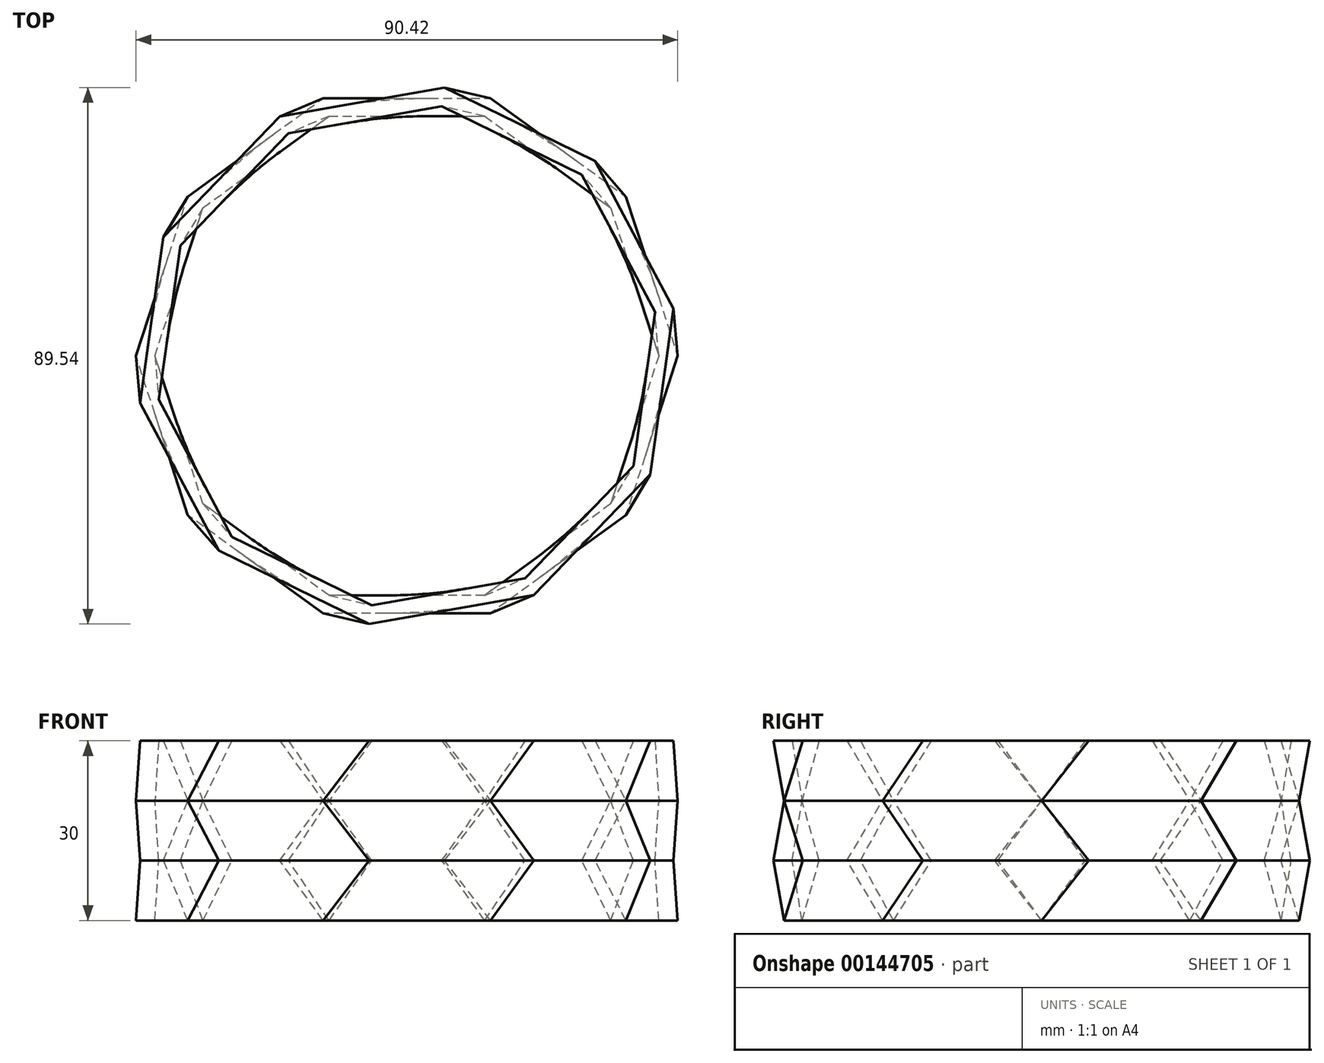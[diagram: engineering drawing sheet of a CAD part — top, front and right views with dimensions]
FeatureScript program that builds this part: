
annotation { "Feature Type Name" : "Feature", "Feature Type Description" : "" }
export const myFeature = defineFeature(function(context is Context, id is Id, definition is map)
    precondition{}
    {
        {
            var Q0;
            Q0=qCreatedBy(makeId("Top.planeOp"),FACE);
            var sketch = newSketch(context, id + "F0", { "sketchPlane" : qUnion([Q0])});
            skCircle(sketch, "E0.cCircle", {"center": v(0, 0) * mm, "radius": 40 * mm, "construction": true});
            skLineSegment(sketch, "E0.0", {"start": v(-13, 40) * mm, "end": v(13, 40) * mm});
            skLineSegment(sketch, "E0.1", {"start": v(13, 40) * mm, "end": v(34.03, 24.72) * mm});
            skLineSegment(sketch, "E0.2", {"start": v(34.03, 24.72) * mm, "end": v(42.06, 0) * mm});
            skLineSegment(sketch, "E0.3", {"start": v(42.06, 0) * mm, "end": v(34.03, -24.72) * mm});
            skLineSegment(sketch, "E0.4", {"start": v(34.03, -24.72) * mm, "end": v(13, -40) * mm});
            skLineSegment(sketch, "E0.5", {"start": v(13, -40) * mm, "end": v(-13, -40) * mm});
            skLineSegment(sketch, "E0.6", {"start": v(-13, -40) * mm, "end": v(-34.03, -24.72) * mm});
            skLineSegment(sketch, "E0.7", {"start": v(-34.03, -24.72) * mm, "end": v(-42.06, 0) * mm});
            skLineSegment(sketch, "E0.8", {"start": v(-42.06, 0) * mm, "end": v(-34.03, 24.72) * mm});
            skLineSegment(sketch, "E0.9", {"start": v(-34.03, 24.72) * mm, "end": v(-13, 40) * mm});
            skPoint(sketch, "E0.0.midPoint", {"position": v(0, 40) * mm});
            skSolve(sketch);
        }
        {
            var Q0;
            Q0=qCreatedBy(makeId("Top.planeOp"),FACE);
            var sketch = newSketch(context, id + "F1", { "sketchPlane" : qUnion([Q0])});
            skLineSegment(sketch, "E1.0", {"start": v(-36.58, 26.58) * mm, "end": v(-13.97, 43) * mm});
            skLineSegment(sketch, "E1.1", {"start": v(-45.21, 0) * mm, "end": v(-36.58, 26.58) * mm});
            skLineSegment(sketch, "E1.2", {"start": v(-13.97, 43) * mm, "end": v(13.97, 43) * mm});
            skLineSegment(sketch, "E1.3", {"start": v(-36.58, -26.58) * mm, "end": v(-45.21, 0) * mm});
            skLineSegment(sketch, "E1.4", {"start": v(-13.97, -43) * mm, "end": v(-36.58, -26.58) * mm});
            skLineSegment(sketch, "E1.5", {"start": v(13.97, -43) * mm, "end": v(-13.97, -43) * mm});
            skLineSegment(sketch, "E1.6", {"start": v(13.97, 43) * mm, "end": v(36.58, 26.58) * mm});
            skLineSegment(sketch, "E1.7", {"start": v(36.58, 26.58) * mm, "end": v(45.21, 0) * mm});
            skLineSegment(sketch, "E1.8", {"start": v(45.21, 0) * mm, "end": v(36.58, -26.58) * mm});
            skLineSegment(sketch, "E1.9", {"start": v(36.58, -26.58) * mm, "end": v(13.97, -43) * mm});
            skSolve(sketch);
        }
        {
            var Q0;
            Q0=makeQuery(id+"F1.imprint","IMPRINT",FACE,{"disambiguationData":[TD([[makeQuery(id+"F1.imprint","IMPRINT",EDGE,{"derivedFrom":sQuery(id+"F1.wireOp",EDGE,"E1.0")}),-1.0]])]});
            cPlane(context, id + "F2", {"entities" : qUnion([Q0]), "cplaneType" : CPlaneType.OFFSET, "offset" : 10 * mm, "width" : 150 * mm, "height" : 150 * mm});
        }
        {
            var Q0;
            Q0=qCreatedBy(id+"F2.planeOp",FACE);
            var sketch = newSketch(context, id + "F3", { "sketchPlane" : qUnion([Q0])});
            skCircle(sketch, "E2.cCircle", {"center": v(0, 0) * mm, "radius": 40 * mm, "construction": true});
            skLineSegment(sketch, "E2.0", {"start": v(-5.85, -41.65) * mm, "end": v(-29.22, -30.25) * mm});
            skLineSegment(sketch, "E2.1", {"start": v(-29.22, -30.25) * mm, "end": v(-41.42, -7.3) * mm});
            skLineSegment(sketch, "E2.2", {"start": v(-41.42, -7.3) * mm, "end": v(-37.8, 18.44) * mm});
            skLineSegment(sketch, "E2.3", {"start": v(-37.8, 18.44) * mm, "end": v(-19.75, 37.14) * mm});
            skLineSegment(sketch, "E2.4", {"start": v(-19.75, 37.14) * mm, "end": v(5.85, 41.65) * mm});
            skLineSegment(sketch, "E2.5", {"start": v(5.85, 41.65) * mm, "end": v(29.22, 30.25) * mm});
            skLineSegment(sketch, "E2.6", {"start": v(29.22, 30.25) * mm, "end": v(41.42, 7.3) * mm});
            skLineSegment(sketch, "E2.7", {"start": v(41.42, 7.3) * mm, "end": v(37.8, -18.44) * mm});
            skLineSegment(sketch, "E2.8", {"start": v(37.8, -18.44) * mm, "end": v(19.75, -37.14) * mm});
            skLineSegment(sketch, "E2.9", {"start": v(19.75, -37.14) * mm, "end": v(-5.85, -41.65) * mm});
            skPoint(sketch, "E2.0.midPoint", {"position": v(-17.53, -35.95) * mm});
            skSolve(sketch);
        }
        {
            var Q0;
            Q0=qCreatedBy(id+"F2.planeOp",FACE);
            var sketch = newSketch(context, id + "F4", { "sketchPlane" : qUnion([Q0])});
            skLineSegment(sketch, "E3.0", {"start": v(-40.64, 19.82) * mm, "end": v(-21.23, 39.92) * mm});
            skLineSegment(sketch, "E3.1", {"start": v(-44.53, -7.85) * mm, "end": v(-40.64, 19.82) * mm});
            skLineSegment(sketch, "E3.2", {"start": v(-21.23, 39.92) * mm, "end": v(6.3, 44.77) * mm});
            skLineSegment(sketch, "E3.3", {"start": v(-31.4, -32.52) * mm, "end": v(-44.53, -7.85) * mm});
            skLineSegment(sketch, "E3.4", {"start": v(-6.3, -44.77) * mm, "end": v(-31.4, -32.52) * mm});
            skLineSegment(sketch, "E3.5", {"start": v(21.23, -39.92) * mm, "end": v(-6.3, -44.77) * mm});
            skLineSegment(sketch, "E3.6", {"start": v(6.3, 44.77) * mm, "end": v(31.4, 32.52) * mm});
            skLineSegment(sketch, "E3.7", {"start": v(31.4, 32.52) * mm, "end": v(44.53, 7.85) * mm});
            skLineSegment(sketch, "E3.8", {"start": v(44.53, 7.85) * mm, "end": v(40.64, -19.82) * mm});
            skLineSegment(sketch, "E3.9", {"start": v(40.64, -19.82) * mm, "end": v(21.23, -39.92) * mm});
            skSolve(sketch);
        }
        {
            var Q0;
            Q0=makeQuery(id+"F0.imprint","IMPRINT",FACE,{"disambiguationData":[TD([[makeQuery(id+"F0.imprint","IMPRINT",EDGE,{"derivedFrom":sQuery(id+"F0.wireOp",EDGE,"E0.0")}),-1.0]])]});
            var Q1;
            Q1=makeQuery(id+"F3.imprint","IMPRINT",FACE,{"disambiguationData":[TD([[makeQuery(id+"F3.imprint","IMPRINT",EDGE,{"derivedFrom":sQuery(id+"F3.wireOp",EDGE,"E2.0")}),-1.0]])]});
            loft(context, id + "F5", {"sheetProfilesArray" : [{ "sheetProfileEntities" : qUnion([Q0]) }, { "sheetProfileEntities" : qUnion([Q1]) }]});
        }
        {
            var Q1;
            Q1=makeQuery(id+"F1.imprint","IMPRINT",FACE,{"disambiguationData":[TD([[makeQuery(id+"F1.imprint","IMPRINT",EDGE,{"derivedFrom":sQuery(id+"F1.wireOp",EDGE,"E1.0")}),-1.0]])]});
            var Q2;
            Q2=makeQuery(id+"F4.imprint","IMPRINT",FACE,{"disambiguationData":[TD([[makeQuery(id+"F4.imprint","IMPRINT",EDGE,{"derivedFrom":sQuery(id+"F4.wireOp",EDGE,"E3.0")}),-1.0]])]});
            loft(context, id + "F6", {"sheetProfilesArray" : [{ "sheetProfileEntities" : qUnion([Q1]) }, { "sheetProfileEntities" : qUnion([Q2]) }]});
        }
        {
            var Q0;
            Q0=makeQuery(id+"F5.opLoft","SWEPT_BODY",BODY,{"disambiguationData":[OSD([makeQuery(id+"F0.imprint","IMPRINT",FACE,{"disambiguationData":[TD([[makeQuery(id+"F0.imprint","IMPRINT",EDGE,{"derivedFrom":sQuery(id+"F0.wireOp",EDGE,"E0.0")}),-1.0]])]}),makeQuery(id+"F3.imprint","IMPRINT",FACE,{"disambiguationData":[TD([[makeQuery(id+"F3.imprint","IMPRINT",EDGE,{"derivedFrom":sQuery(id+"F3.wireOp",EDGE,"E2.0")}),-1.0]])]})])]});
            var Q1;
            Q1=makeQuery(id+"F6.opLoft","SWEPT_BODY",BODY,{"disambiguationData":[OSD([makeQuery(id+"F1.imprint","IMPRINT",FACE,{"disambiguationData":[TD([[makeQuery(id+"F1.imprint","IMPRINT",EDGE,{"derivedFrom":sQuery(id+"F1.wireOp",EDGE,"E1.0")}),-1.0]])]}),makeQuery(id+"F4.imprint","IMPRINT",FACE,{"disambiguationData":[TD([[makeQuery(id+"F4.imprint","IMPRINT",EDGE,{"derivedFrom":sQuery(id+"F4.wireOp",EDGE,"E3.0")}),-1.0]])]})])]});
            booleanBodies(context, id + "F7", {"operationType" : BooleanOperationType.SUBTRACTION, "tools" : qUnion([Q0]), "targets" : qUnion([Q1])});
        }
        {
            var Q0;
            Q0=makeQuery(id+"F6.opLoft","CAP_FACE",FACE,{"disambiguationData":[OSD([makeQuery(id+"F4.imprint","IMPRINT",FACE,{"disambiguationData":[TD([[makeQuery(id+"F4.imprint","IMPRINT",EDGE,{"derivedFrom":sQuery(id+"F4.wireOp",EDGE,"E3.0")}),-1.0]])]})])],"isStart":true});
            cPlane(context, id + "F8", {"entities" : qUnion([Q0]), "cplaneType" : CPlaneType.OFFSET, "offset" : 10 * mm, "width" : 150 * mm, "height" : 150 * mm});
        }
        {
            var Q0;
            Q0=qCreatedBy(id+"F8.planeOp",FACE);
            var sketch = newSketch(context, id + "F9", { "sketchPlane" : qUnion([Q0])});
            skCircle(sketch, "E4.cCircle", {"center": v(0, 0) * mm, "radius": 40 * mm, "construction": true});
            skLineSegment(sketch, "E4.0", {"start": v(-13, 40) * mm, "end": v(13, 40) * mm});
            skLineSegment(sketch, "E4.1", {"start": v(13, 40) * mm, "end": v(34.03, 24.72) * mm});
            skLineSegment(sketch, "E4.2", {"start": v(34.03, 24.72) * mm, "end": v(42.06, 0) * mm});
            skLineSegment(sketch, "E4.3", {"start": v(42.06, 0) * mm, "end": v(34.03, -24.72) * mm});
            skLineSegment(sketch, "E4.4", {"start": v(34.03, -24.72) * mm, "end": v(13, -40) * mm});
            skLineSegment(sketch, "E4.5", {"start": v(13, -40) * mm, "end": v(-13, -40) * mm});
            skLineSegment(sketch, "E4.6", {"start": v(-13, -40) * mm, "end": v(-34.03, -24.72) * mm});
            skLineSegment(sketch, "E4.7", {"start": v(-34.03, -24.72) * mm, "end": v(-42.06, 0) * mm});
            skLineSegment(sketch, "E4.8", {"start": v(-42.06, 0) * mm, "end": v(-34.03, 24.72) * mm});
            skLineSegment(sketch, "E4.9", {"start": v(-34.03, 24.72) * mm, "end": v(-13, 40) * mm});
            skPoint(sketch, "E4.0.midPoint", {"position": v(0, 40) * mm});
            skSolve(sketch);
        }
        {
            var Q0;
            Q0=qCreatedBy(id+"F8.planeOp",FACE);
            var sketch = newSketch(context, id + "F10", { "sketchPlane" : qUnion([Q0])});
            skLineSegment(sketch, "E5.0", {"start": v(-36.58, 26.58) * mm, "end": v(-13.97, 43) * mm});
            skLineSegment(sketch, "E5.1", {"start": v(-45.21, 0) * mm, "end": v(-36.58, 26.58) * mm});
            skLineSegment(sketch, "E5.2", {"start": v(-13.97, 43) * mm, "end": v(13.97, 43) * mm});
            skLineSegment(sketch, "E5.3", {"start": v(-36.58, -26.58) * mm, "end": v(-45.21, 0) * mm});
            skLineSegment(sketch, "E5.4", {"start": v(-13.97, -43) * mm, "end": v(-36.58, -26.58) * mm});
            skLineSegment(sketch, "E5.5", {"start": v(13.97, -43) * mm, "end": v(-13.97, -43) * mm});
            skLineSegment(sketch, "E5.6", {"start": v(13.97, 43) * mm, "end": v(36.58, 26.58) * mm});
            skLineSegment(sketch, "E5.7", {"start": v(36.58, 26.58) * mm, "end": v(45.21, 0) * mm});
            skLineSegment(sketch, "E5.8", {"start": v(45.21, 0) * mm, "end": v(36.58, -26.58) * mm});
            skLineSegment(sketch, "E5.9", {"start": v(36.58, -26.58) * mm, "end": v(13.97, -43) * mm});
            skSolve(sketch);
        }
        {
            var Q0;
            Q0=makeQuery(id+"F4.imprint","IMPRINT",FACE,{"disambiguationData":[TD([[makeQuery(id+"F4.imprint","IMPRINT",EDGE,{"derivedFrom":sQuery(id+"F4.wireOp",EDGE,"E3.0")}),-1.0]])]});
            var sketch = newSketch(context, id + "F11", { "sketchPlane" : qUnion([Q0])});
            skLineSegment(sketch, "E6.0", {"start": v(-31.4, -32.52) * mm, "end": v(-44.53, -7.85) * mm});
            skLineSegment(sketch, "E7.0", {"start": v(-6.3, -44.77) * mm, "end": v(-31.4, -32.52) * mm});
            skLineSegment(sketch, "E8.0", {"start": v(21.23, -39.92) * mm, "end": v(-6.3, -44.77) * mm});
            skLineSegment(sketch, "E9.0", {"start": v(40.64, -19.82) * mm, "end": v(21.23, -39.92) * mm});
            skLineSegment(sketch, "E10.0", {"start": v(44.53, 7.85) * mm, "end": v(40.64, -19.82) * mm});
            skLineSegment(sketch, "E11.0", {"start": v(31.4, 32.52) * mm, "end": v(44.53, 7.85) * mm});
            skLineSegment(sketch, "E12.0", {"start": v(6.3, 44.77) * mm, "end": v(31.4, 32.52) * mm});
            skLineSegment(sketch, "E13.0", {"start": v(-21.23, 39.92) * mm, "end": v(6.3, 44.77) * mm});
            skLineSegment(sketch, "E14.0", {"start": v(-40.64, 19.82) * mm, "end": v(-21.23, 39.92) * mm});
            skLineSegment(sketch, "E15.0", {"start": v(-44.53, -7.85) * mm, "end": v(-40.64, 19.82) * mm});
            skSolve(sketch);
        }
        {
            var Q0;
            Q0=qCreatedBy(id+"F2.planeOp",FACE);
            var sketch = newSketch(context, id + "F12", { "sketchPlane" : qUnion([Q0])});
            skLineSegment(sketch, "E16.0", {"start": v(-37.8, 18.44) * mm, "end": v(-41.42, -7.3) * mm});
            skLineSegment(sketch, "E17.0", {"start": v(-19.75, 37.14) * mm, "end": v(-37.8, 18.44) * mm});
            skLineSegment(sketch, "E18.0", {"start": v(29.22, 30.25) * mm, "end": v(5.85, 41.65) * mm});
            skLineSegment(sketch, "E19.0", {"start": v(5.85, 41.65) * mm, "end": v(-19.75, 37.14) * mm});
            skLineSegment(sketch, "E20.0", {"start": v(41.42, 7.3) * mm, "end": v(29.22, 30.25) * mm});
            skLineSegment(sketch, "E21.0", {"start": v(37.8, -18.44) * mm, "end": v(41.42, 7.3) * mm});
            skLineSegment(sketch, "E22.0", {"start": v(19.75, -37.14) * mm, "end": v(37.8, -18.44) * mm});
            skLineSegment(sketch, "E23.0", {"start": v(-5.85, -41.65) * mm, "end": v(19.75, -37.14) * mm});
            skLineSegment(sketch, "E24.0", {"start": v(-29.22, -30.25) * mm, "end": v(-5.85, -41.65) * mm});
            skLineSegment(sketch, "E25.0", {"start": v(-41.42, -7.3) * mm, "end": v(-29.22, -30.25) * mm});
            skSolve(sketch);
        }
        {
            var Q0;
            Q0=makeQuery(id+"F12.imprint","IMPRINT",FACE,{"disambiguationData":[TD([[makeQuery(id+"F12.imprint","IMPRINT",EDGE,{"derivedFrom":sQuery(id+"F12.wireOp",EDGE,"E16.0")}),1.0]])]});
            var Q1;
            Q1=makeQuery(id+"F9.imprint","IMPRINT",FACE,{"disambiguationData":[TD([[makeQuery(id+"F9.imprint","IMPRINT",EDGE,{"derivedFrom":sQuery(id+"F9.wireOp",EDGE,"E4.0")}),-1.0]])]});
            loft(context, id + "F13", {"sheetProfilesArray" : [{ "sheetProfileEntities" : qUnion([Q0]) }, { "sheetProfileEntities" : qUnion([Q1]) }]});
        }
        {
            var Q0;
            Q0=makeQuery(id+"F11.imprint","IMPRINT",FACE,{"disambiguationData":[TD([[makeQuery(id+"F11.imprint","IMPRINT",EDGE,{"derivedFrom":sQuery(id+"F11.wireOp",EDGE,"E7.0")}),-1.0]])]});
            var Q1;
            Q1=makeQuery(id+"F10.imprint","IMPRINT",FACE,{"disambiguationData":[TD([[makeQuery(id+"F10.imprint","IMPRINT",EDGE,{"derivedFrom":sQuery(id+"F10.wireOp",EDGE,"E5.0")}),-1.0]])]});
            loft(context, id + "F14", {"sheetProfilesArray" : [{ "sheetProfileEntities" : qUnion([Q0]) }, { "sheetProfileEntities" : qUnion([Q1]) }]});
        }
        {
            var Q0;
            Q0=makeQuery(id+"F13.opLoft","SWEPT_BODY",BODY,{"disambiguationData":[OSD([makeQuery(id+"F9.imprint","IMPRINT",FACE,{"disambiguationData":[TD([[makeQuery(id+"F9.imprint","IMPRINT",EDGE,{"derivedFrom":sQuery(id+"F9.wireOp",EDGE,"E4.0")}),-1.0]])]}),makeQuery(id+"F12.imprint","IMPRINT",FACE,{"disambiguationData":[TD([[makeQuery(id+"F12.imprint","IMPRINT",EDGE,{"derivedFrom":sQuery(id+"F12.wireOp",EDGE,"E16.0")}),1.0]])]})])]});
            var Q1;
            Q1=makeQuery(id+"F14.opLoft","SWEPT_BODY",BODY,{"disambiguationData":[OSD([makeQuery(id+"F10.imprint","IMPRINT",FACE,{"disambiguationData":[TD([[makeQuery(id+"F10.imprint","IMPRINT",EDGE,{"derivedFrom":sQuery(id+"F10.wireOp",EDGE,"E5.0")}),-1.0]])]}),makeQuery(id+"F11.imprint","IMPRINT",FACE,{"disambiguationData":[TD([[makeQuery(id+"F11.imprint","IMPRINT",EDGE,{"derivedFrom":sQuery(id+"F11.wireOp",EDGE,"E7.0")}),-1.0]])]})])]});
            booleanBodies(context, id + "F15", {"operationType" : BooleanOperationType.SUBTRACTION, "tools" : qUnion([Q0]), "targets" : qUnion([Q1])});
        }
        {
            var Q0;
            Q0=makeQuery(id+"F14.opLoft","SWEPT_BODY",BODY,{"disambiguationData":[OSD([makeQuery(id+"F10.imprint","IMPRINT",FACE,{"disambiguationData":[TD([[makeQuery(id+"F10.imprint","IMPRINT",EDGE,{"derivedFrom":sQuery(id+"F10.wireOp",EDGE,"E5.0")}),-1.0]])]}),makeQuery(id+"F11.imprint","IMPRINT",FACE,{"disambiguationData":[TD([[makeQuery(id+"F11.imprint","IMPRINT",EDGE,{"derivedFrom":sQuery(id+"F11.wireOp",EDGE,"E7.0")}),-1.0]])]})])]});
            var Q1;
            Q1=makeQuery(id+"F10.imprint","IMPRINT",FACE,{"disambiguationData":[TD([[makeQuery(id+"F10.imprint","IMPRINT",EDGE,{"derivedFrom":sQuery(id+"F10.wireOp",EDGE,"E5.0")}),-1.0]])]});
            mirror(context, id + "F16", {"operationType" : NewBodyOperationType.ADD, "entities" : qUnion([Q0]), "mirrorPlane" : qUnion([Q1])});
        }
    });
